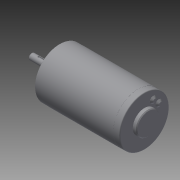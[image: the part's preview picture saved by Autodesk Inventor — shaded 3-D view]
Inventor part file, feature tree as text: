
AUTODESK INVENTOR PART (.ipt)
format: ipt  version: 2014 (Build 180170000, 170)  size: 150,016 bytes
history: native  units: in
note: dims shown in document units (in); Inventor stores cm internally (conversion verified against a paired STEP export)
features: chamfer x1, other x1, imported_body x1
ambient origin geometry x8: Origin, YZ Plane, XZ Plane, XY Plane, X Axis, Y Axis, Z Axis, Center Point
bodies: Body1 (feature_tree)
feature tree (3):
  chamfer  "Chamfer3"  [1 undecoded]
  other  "Cim motor1"
  imported_body  "Base1"
note: 1 required parameter value undecoded (feature->parameter linkage not recoverable at this tier; creation-order binding heuristic only, values carry confidence <= 0.55)
